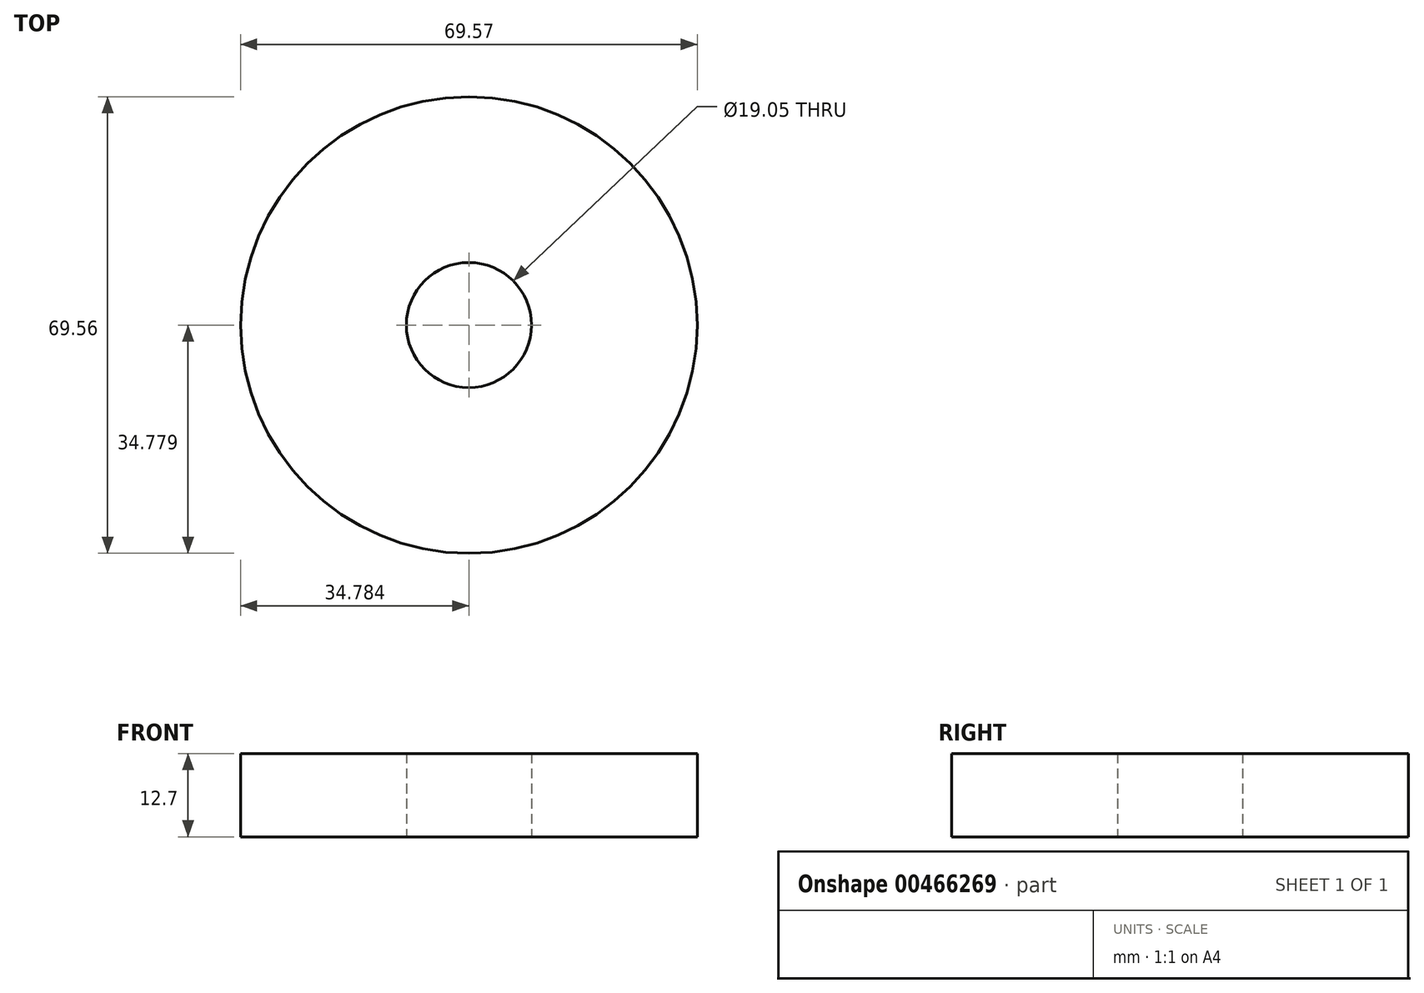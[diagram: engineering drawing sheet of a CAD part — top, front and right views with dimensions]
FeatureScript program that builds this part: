
annotation { "Feature Type Name" : "Feature", "Feature Type Description" : "" }
export const myFeature = defineFeature(function(context is Context, id is Id, definition is map)
    precondition{}
    {
        {
            var Q0;
            Q0=qCreatedBy(makeId("Top.planeOp"),FACE);
            var sketch = newSketch(context, id + "F0", { "sketchPlane" : qUnion([Q0])});
            skCircle(sketch, "E0", {"center": v(-28.17, -50.24) * mm, "radius": 34.78 * mm});
            skSolve(sketch);
        }
        {
            var Q0;
            Q0=makeQuery(id+"F0.imprint","IMPRINT",FACE,{"disambiguationData":[TD([[makeQuery(id+"F0.imprint","IMPRINT",EDGE,{"derivedFrom":sQuery(id+"F0.wireOp",EDGE,"E0")}),1.0]])]});
            extrude(context, id + "F1", {"entities" : qUnion([Q0]), "depth" : 12.7 * mm});
        }
        {
            var Q0;
            Q0=sQuery(id+"F0.wireOp",VERTEX,"E0.center");
            var Q1;
            Q1=makeQuery(id+"F1.opExtrude","SWEPT_BODY",BODY,{"disambiguationData":[OSD([sQuery(id+"F0.wireOp",EDGE,"E0")])]});
            hole(context, id + "F2", {"style" : HoleStyle.SIMPLE, "endStyle" : HoleEndStyle.THROUGH, "oppositeDirection" : true, "holeDiameter" : 19.05 * mm, "isTappedThrough" : true, "tappedDepth" : 12.7 * mm, "tapClearance" : 3, "locations" : qUnion([Q0]), "scope" : qUnion([Q1])});
        }
        {
            var Q0;
            Q0=sQuery(id+"F0.wireOp",VERTEX,"E0.center");
            var Q1;
            Q1=makeQuery(id+"F1.opExtrude","SWEPT_BODY",BODY,{"disambiguationData":[OSD([sQuery(id+"F0.wireOp",EDGE,"E0")])]});
            hole(context, id + "F3", {"style" : HoleStyle.SIMPLE, "endStyle" : HoleEndStyle.BLIND, "oppositeDirection" : true, "standardTappedOrClearance" : lookupTablePath({ "standard" : "ISO", "fit" : "Normal", "size" : "M5", "type" : "Clearance" }), "standardBlindInLast" : lookupTablePath({ "fit" : "Standard", "standard" : "ISO", "size" : "M5", "type" : "Clearance" }), "holeDiameter" : 5.5 * mm, "holeDepth" : 7.62 * mm, "isTappedThrough" : true, "tappedDepth" : 12.7 * mm, "tapClearance" : 3, "locations" : qUnion([Q0]), "scope" : qUnion([Q1])});
        }
    });
